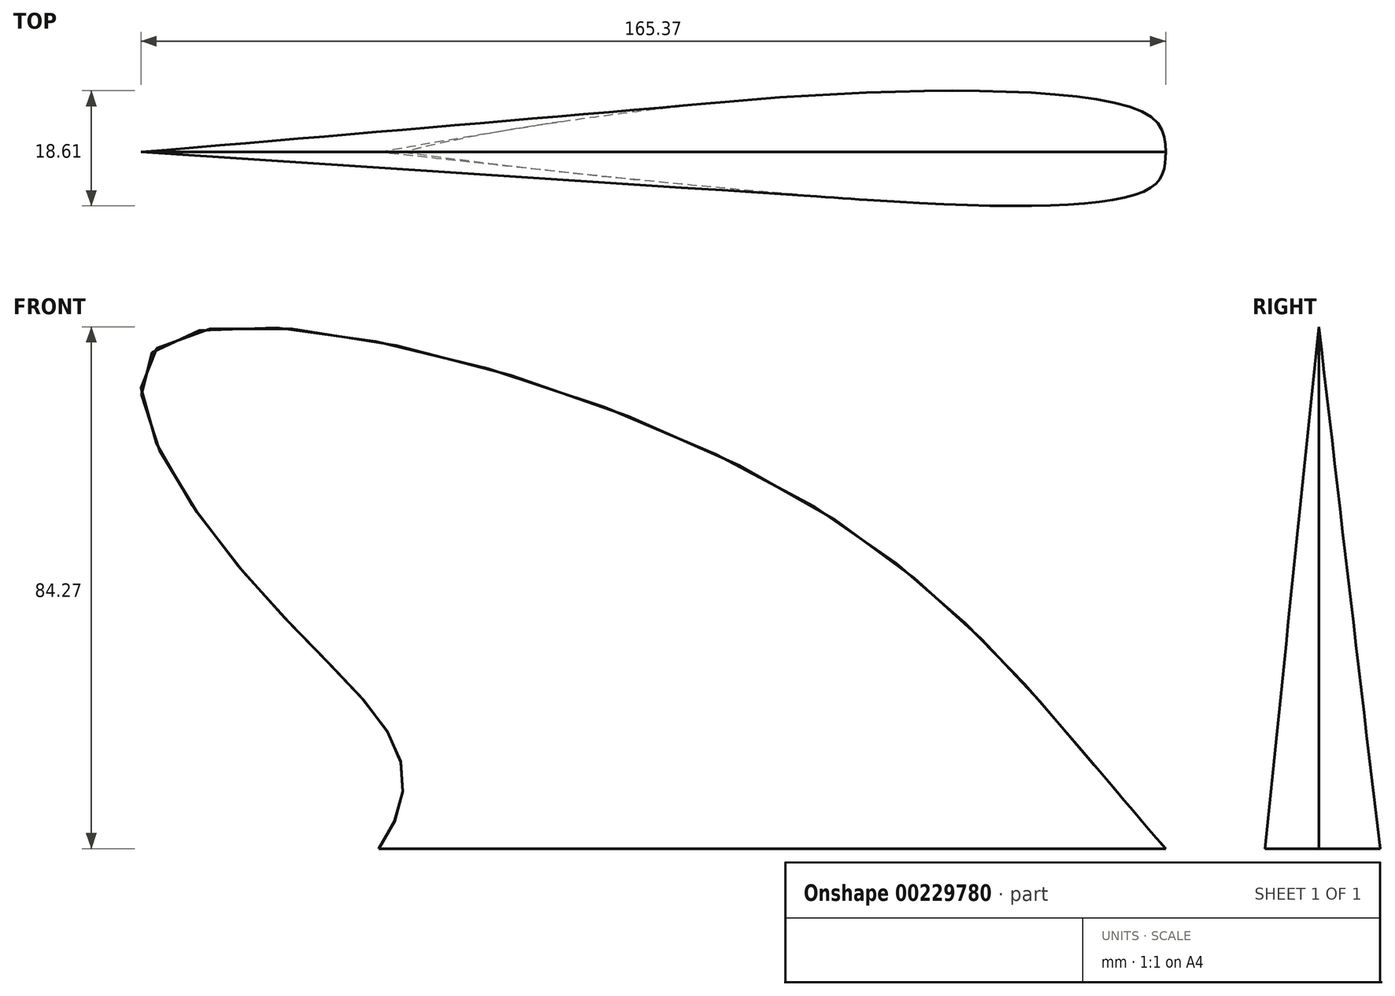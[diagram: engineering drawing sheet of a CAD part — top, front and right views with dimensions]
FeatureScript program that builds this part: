
annotation { "Feature Type Name" : "Feature", "Feature Type Description" : "" }
export const myFeature = defineFeature(function(context is Context, id is Id, definition is map)
    precondition{}
    {
        {
            var Q0;
            Q0=qCreatedBy(makeId("Top.planeOp"),FACE);
            var sketch = newSketch(context, id + "F0", { "sketchPlane" : qUnion([Q0])});
            skFitSpline(sketch, "E0", {"points": [v(-63.86, 0) * mm, v(0, 8.76) * mm, v(60.58, 5.84) * mm, v(63.14, 0) * mm], "startDerivative": vector(133.68, 23.78) * mm, "endDerivative": vector(1.92, -46.33) * mm});
            skFitSpline(sketch, "E1", {"points": [v(63.14, 0) * mm, v(60.58, -5.84) * mm, v(-63.86, 0) * mm], "startDerivative": vector(-1.05, -35.23) * mm, "endDerivative": vector(-209.17, 22.99) * mm});
            skSolve(sketch);
        }
        {
            var Q0;
            Q0=qCreatedBy(makeId("Front.planeOp"),FACE);
            var sketch = newSketch(context, id + "F1", { "sketchPlane" : qUnion([Q0])});
            skFitSpline(sketch, "E2", {"points": [v(63.14, 0) * mm, v(0, 58.92) * mm, v(-100.4, 80.08) * mm, v(-85.47, 44.4) * mm, v(-63.07, 19.92) * mm, v(-59.94, 9.58) * mm, v(-63.86, 0) * mm], "startDerivative": vector(-222.72, 248.88) * mm, "endDerivative": vector(-76.68, -104.58) * mm});
            skSolve(sketch);
        }
        {
            var Q0;
            Q0=sQuery(id+"F0.wireOp",EDGE,"E0");
            var Q1;
            Q1=sQuery(id+"F1.wireOp",EDGE,"E2");
            loft(context, id + "F2", {"bodyType" : ToolBodyType.SURFACE, "wireProfilesArray" : [{ "wireProfileEntities" : qUnion([Q0]) }, { "wireProfileEntities" : qUnion([Q1]) }]});
        }
        {
            var Q0;
            Q0=sQuery(id+"F1.wireOp",EDGE,"E2");
            var Q1;
            Q1=sQuery(id+"F0.wireOp",EDGE,"E1");
            loft(context, id + "F3", {"bodyType" : ToolBodyType.SURFACE, "wireProfilesArray" : [{ "wireProfileEntities" : qUnion([Q0]) }, { "wireProfileEntities" : qUnion([Q1]) }]});
        }
    });
